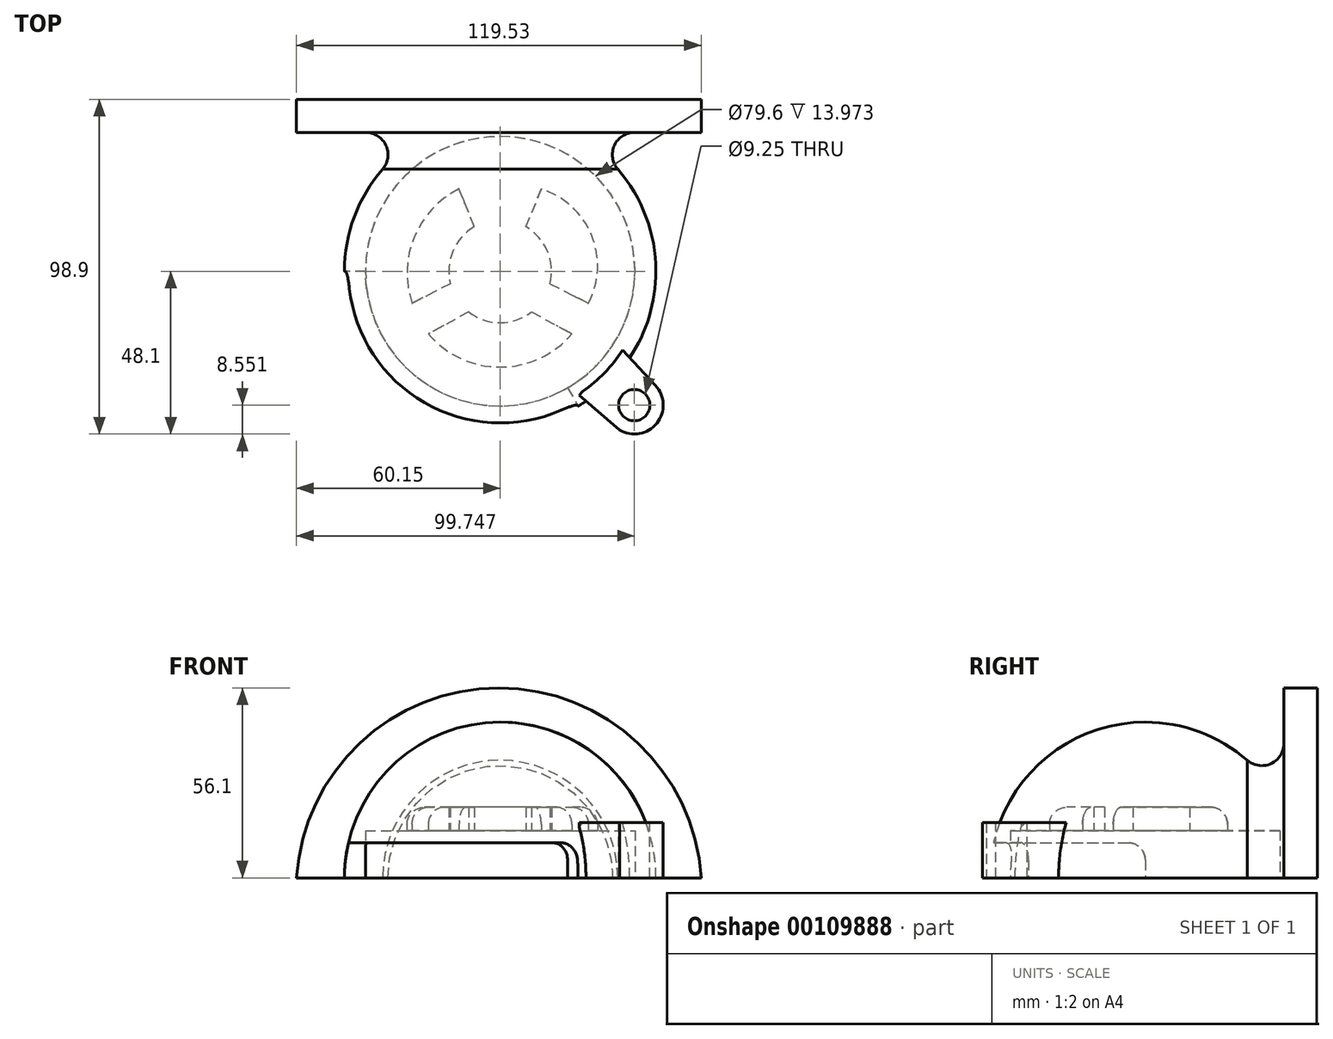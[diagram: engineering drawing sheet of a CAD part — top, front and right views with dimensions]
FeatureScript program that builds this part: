
annotation { "Feature Type Name" : "Feature", "Feature Type Description" : "" }
export const myFeature = defineFeature(function(context is Context, id is Id, definition is map)
    precondition{}
    {
        {
            var Q0;
            Q0=qCreatedBy(makeId("Front.planeOp"),FACE);
            var sketch = newSketch(context, id + "F0", { "sketchPlane" : qUnion([Q0])});
            skArc(sketch, "E0", {"start": v(46, 0) * mm, "mid": v(32.53, 32.53) * mm, "end": v(0, 46) * mm});
            skLineSegment(sketch, "E1", {"start": v(0, 41.14) * mm, "end": v(0, 46) * mm});
            skLineSegment(sketch, "E2", {"start": v(0, 70.48) * mm, "end": v(0, -35.62) * mm});
            skLineSegment(sketch, "E3", {"start": v(0, 46) * mm, "end": v(0, 0) * mm});
            skLineSegment(sketch, "E4", {"start": v(46, 0) * mm, "end": v(0, 0) * mm});
            skSolve(sketch);
        }
        {
            var Q0;
            {var subQ0=sQuery(id+"F0.wireOp",EDGE,"E0");Q0=makeQuery(id+"F0.imprint","IMPRINT",FACE,{"disambiguationData":[TD([[makeQuery(id+"F0.imprint","IMPRINT",EDGE,{"derivedFrom":subQ0}),1.0]])]});}
            var Q1;
            Q1=sQuery(id+"F0.wireOp",EDGE,"E2");
            revolve(context, id + "F1", {"entities" : qUnion([Q0]), "axis" : qUnion([Q1]), "revolveType" : RevolveType.FULL});
        }
        {
            var Q0;
            Q0=qCreatedBy(makeId("Front.planeOp"),FACE);
            var sketch = newSketch(context, id + "F2", { "sketchPlane" : qUnion([Q0])});
            skArc(sketch, "E5", {"start": v(-47.2, 10.38) * mm, "mid": v(-48.92, 3.9) * mm, "end": v(-49.05, -2.81) * mm});
            skArc(sketch, "E6", {"start": v(-36.62, 10.38) * mm, "mid": v(-39.35, 4.06) * mm, "end": v(-39.58, -2.81) * mm});
            skLineSegment(sketch, "E7", {"start": v(-36.62, 10.38) * mm, "end": v(-47.2, 10.38) * mm});
            skLineSegment(sketch, "E8", {"start": v(-39.58, -2.81) * mm, "end": v(-49.05, -2.81) * mm});
            skLineSegment(sketch, "E9", {"start": v(0, 65.03) * mm, "end": v(0, -45.95) * mm});
            skSolve(sketch);
        }
        {
            var Q0;
            Q0=makeQuery(id+"F2.imprint","IMPRINT",FACE,{"disambiguationData":[TD([[makeQuery(id+"F2.imprint","IMPRINT",EDGE,{"derivedFrom":sQuery(id+"F2.wireOp",EDGE,"E5")}),1.0]])]});
            var Q1;
            Q1=sQuery(id+"F2.wireOp",EDGE,"E9");
            revolve(context, id + "F3", {"operationType" : NewBodyOperationType.REMOVE, "entities" : qUnion([Q0]), "axis" : qUnion([Q1]), "revolveType" : RevolveType.ONE_DIRECTION, "oppositeDirection" : true, "angle" : 120 * degree});
        }
        {
            var Q0;
            Q0=makeQuery(id+"F1.opRevolve","SWEPT_FACE",FACE,{"disambiguationData":[OSD([sQuery(id+"F0.wireOp",EDGE,"E4")])]});
            var sketch = newSketch(context, id + "F4", { "sketchPlane" : qUnion([Q0])});
            skSolve(sketch);
        }
        {
            var Q0;
            {var subQ0=sQuery(id+"F0.wireOp",EDGE,"E4");Q0=makeQuery(id+"F4.imprint","IMPRINT",FACE,{"disambiguationData":[TD([[makeQuery(id+"F4.imprint","IMPRINT",EDGE,{"derivedFrom":makeQuery(id+"F1.opRevolve","SWEPT_EDGE",EDGE,{"disambiguationData":[OSD([sQuery(id+"F0.wireOp",EDGE,"E0"),subQ0])]})}),-1.0]])]});}
            var sketch = newSketch(context, id + "F5", { "sketchPlane" : qUnion([Q0])});
            skCircle(sketch, "E10", {"center": v(0, 0) * mm, "radius": 39.8 * mm});
            skSolve(sketch);
        }
        {
            var Q0;
            Q0 = qSketchRegion(id + "F5", true);
            extrude(context, id + "F6", {"entities" : qUnion([Q0]), "operationType" : NewBodyOperationType.REMOVE, "oppositeDirection" : true, "depth" : 13.97 * mm});
        }
        {
            var Q0;
            Q0=makeQuery(id+"F3.boolean.opBoolean","COPY",EDGE,{"derivedFrom":makeQuery(id+"F3.opRevolve","CAP_EDGE",EDGE,{"disambiguationData":[OSD([sQuery(id+"F2.wireOp",EDGE,"E7")])],"isStart":true})});
            var Q1;
            Q1=makeQuery(id+"F3.boolean.opBoolean","COPY",EDGE,{"derivedFrom":makeQuery(id+"F3.opRevolve","CAP_EDGE",EDGE,{"disambiguationData":[OSD([sQuery(id+"F2.wireOp",EDGE,"E7")])],"isStart":false})});
            fillet(context, id + "F7", {"entities" : qUnion([Q0, Q1]), "radius" : 5.08 * mm, "tangentPropagation" : true, "allowEdgeOverflow" : false});
        }
        {
            var Q0;
            Q0=makeQuery(id+"F6.boolean.opBoolean","COPY",FACE,{"derivedFrom":makeQuery(id+"F6.opExtrude","CAP_FACE",FACE,{"disambiguationData":[OSD([sQuery(id+"F5.wireOp",EDGE,"E10")])],"isStart":false})});
            var sketch = newSketch(context, id + "F8", { "sketchPlane" : qUnion([Q0])});
            skCircle(sketch, "E11", {"center": v(0, 0) * mm, "radius": 15.18 * mm});
            skLineSegment(sketch, "E12", {"start": v(9.26, 12.02) * mm, "end": v(21.2, 18.5) * mm});
            skLineSegment(sketch, "E13.MirrorCS", {"start": v(-9.26, 12.02) * mm, "end": v(-21.2, 18.5) * mm});
            skArc(sketch, "E14", {"start": v(21.2, 18.5) * mm, "mid": v(0, 28.3) * mm, "end": v(-21.2, 18.5) * mm});
            skLineSegment(sketch, "E15", {"start": v(14.72, 3.68) * mm, "end": v(26.03, 9.45) * mm});
            skLineSegment(sketch, "E16.MirrorCS", {"start": v(-14.72, 3.68) * mm, "end": v(-26.03, 9.45) * mm});
            skArc(sketch, "E17", {"start": v(-26.03, 9.45) * mm, "mid": v(-25.42, -10.03) * mm, "end": v(-12.15, -24.3) * mm});
            skLineSegment(sketch, "E18", {"start": v(-7.61, -13.13) * mm, "end": v(-12.15, -24.3) * mm});
            skLineSegment(sketch, "E19.MirrorCS", {"start": v(7.61, -13.13) * mm, "end": v(12.15, -24.3) * mm});
            skArc(sketch, "E20", {"start": v(12.15, -24.3) * mm, "mid": v(27, -10.68) * mm, "end": v(26.03, 9.45) * mm});
            skSolve(sketch);
        }
        {
            var Q0;
            {var subQ0=sQuery(id+"F8.wireOp",EDGE,"E12");Q0=makeQuery(id+"F8.imprint","IMPRINT",FACE,{"disambiguationData":[TD([[makeQuery(id+"F8.imprint","IMPRINT",EDGE,{"derivedFrom":subQ0}),1.0]])]});}
            var Q1;
            {var subQ0=sQuery(id+"F8.wireOp",EDGE,"E16.MirrorCS");Q1=makeQuery(id+"F8.imprint","IMPRINT",FACE,{"disambiguationData":[TD([[makeQuery(id+"F8.imprint","IMPRINT",EDGE,{"derivedFrom":subQ0}),1.0]])]});}
            var Q2;
            {var subQ0=sQuery(id+"F8.wireOp",EDGE,"E15");Q2=makeQuery(id+"F8.imprint","IMPRINT",FACE,{"disambiguationData":[TD([[makeQuery(id+"F8.imprint","IMPRINT",EDGE,{"derivedFrom":subQ0}),-1.0]])]});}
            extrude(context, id + "F9", {"entities" : qUnion([Q0, Q1, Q2]), "operationType" : NewBodyOperationType.REMOVE, "oppositeDirection" : true, "depth" : 6.89 * mm});
        }
        {
            var Q0;
            Q0=makeQuery(id+"F9.boolean.opBoolean","COPY",EDGE,{"derivedFrom":makeQuery(id+"F9.opExtrude","CAP_EDGE",EDGE,{"disambiguationData":[OSD([sQuery(id+"F8.wireOp",EDGE,"E14")])],"isStart":false})});
            var Q1;
            Q1=makeQuery(id+"F9.boolean.opBoolean","COPY",EDGE,{"derivedFrom":makeQuery(id+"F9.opExtrude","CAP_EDGE",EDGE,{"disambiguationData":[OSD([sQuery(id+"F8.wireOp",EDGE,"E20")])],"isStart":false})});
            var Q2;
            Q2=makeQuery(id+"F9.boolean.opBoolean","COPY",EDGE,{"derivedFrom":makeQuery(id+"F9.opExtrude","CAP_EDGE",EDGE,{"disambiguationData":[OSD([sQuery(id+"F8.wireOp",EDGE,"E17")])],"isStart":false})});
            fillet(context, id + "F10", {"entities" : qUnion([Q0, Q1, Q2]), "radius" : 5.08 * mm, "tangentPropagation" : true, "allowEdgeOverflow" : false});
        }
        {
            var Q0;
            Q0=qCreatedBy(makeId("Front.planeOp"),FACE);
            cPlane(context, id + "F11", {"entities" : qUnion([Q0]), "cplaneType" : CPlaneType.OFFSET, "offset" : 50.8 * mm, "oppositeDirection" : true, "width" : 152.4 * mm, "height" : 152.4 * mm});
        }
        {
            var Q0;
            Q0=qCreatedBy(id+"F11.planeOp",FACE);
            var sketch = newSketch(context, id + "F12", { "sketchPlane" : qUnion([Q0])});
            skArc(sketch, "E21", {"start": v(59.38, 0) * mm, "mid": v(-0.39, 56.1) * mm, "end": v(-60.15, 0) * mm});
            skLineSegment(sketch, "E22", {"start": v(59.38, 0) * mm, "end": v(-60.15, 0) * mm});
            skSolve(sketch);
        }
        {
            var Q0;
            Q0=makeQuery(id+"F12.imprint","IMPRINT",FACE,{"disambiguationData":[TD([[makeQuery(id+"F12.imprint","IMPRINT",EDGE,{"derivedFrom":sQuery(id+"F12.wireOp",EDGE,"E21")}),1.0]])]});
            var Q1;
            Q1=makeQuery(id+"F1.opRevolve","SWEPT_BODY",BODY,{"disambiguationData":[OSD([sQuery(id+"F0.wireOp",EDGE,"E0"),sQuery(id+"F0.wireOp",EDGE,"E3"),sQuery(id+"F0.wireOp",EDGE,"E4")])]});
            extrude(context, id + "F13", {"entities" : qUnion([Q0]), "operationType" : NewBodyOperationType.ADD, "endBoundEntityBody" : qUnion([Q1]), "depth" : 9.82 * mm});
        }
        {
            var Q0;
            Q0=makeQuery(id+"F13.boolean.opBoolean","INTERSECT",EDGE,{"derivedFrom":[makeQuery(id+"F1.opRevolve","SWEPT_FACE",FACE,{"disambiguationData":[OSD([sQuery(id+"F0.wireOp",EDGE,"E0")])]}),makeQuery(id+"F13.opExtrude","CAP_FACE",FACE,{"disambiguationData":[OSD([sQuery(id+"F12.wireOp",EDGE,"E21"),sQuery(id+"F12.wireOp",EDGE,"E22")])],"isStart":false})]});
            fillet(context, id + "F14", {"entities" : qUnion([Q0]), "radius" : 6.54 * mm, "tangentPropagation" : true, "allowEdgeOverflow" : false});
        }
        {
            var Q0;
            Q0=qCreatedBy(makeId("Top.planeOp"),FACE);
            var sketch = newSketch(context, id + "F15", { "sketchPlane" : qUnion([Q0])});
            skArc(sketch, "E23", {"start": v(32.95, -44.93) * mm, "mid": v(45.21, -46) * mm, "end": v(45.84, -33.7) * mm});
            skLineSegment(sketch, "E24", {"start": v(35.3, -46.94) * mm, "end": v(23.33, -36.69) * mm});
            skLineSegment(sketch, "E25", {"start": v(45.84, -33.7) * mm, "end": v(35.3, -22.46) * mm});
            skLineSegment(sketch, "E26", {"start": v(35.3, -22.46) * mm, "end": v(23.33, -36.69) * mm});
            skSolve(sketch);
        }
        {
            var Q0;
            {var subQ0=sQuery(id+"F15.wireOp",EDGE,"E25");Q0=makeQuery(id+"F15.imprint","IMPRINT",FACE,{"disambiguationData":[TD([[makeQuery(id+"F15.imprint","IMPRINT",EDGE,{"derivedFrom":subQ0}),1.0]])]});}
            extrude(context, id + "F16", {"entities" : qUnion([Q0]), "operationType" : NewBodyOperationType.ADD, "depth" : 16.3 * mm});
        }
        {
            var Q0;
            Q0=makeQuery(id+"F16.opExtrude","CAP_FACE",FACE,{"disambiguationData":[OSD([sQuery(id+"F15.wireOp",EDGE,"E23"),sQuery(id+"F15.wireOp",EDGE,"E24"),sQuery(id+"F15.wireOp",EDGE,"E25"),sQuery(id+"F15.wireOp",EDGE,"E26")])],"isStart":false});
            var sketch = newSketch(context, id + "F17", { "sketchPlane" : qUnion([Q0])});
            skCircle(sketch, "E27", {"center": v(39.6, -39.55) * mm, "radius": 4.62 * mm});
            skSolve(sketch);
        }
        {
            var Q0;
            Q0=makeQuery(id+"F17.imprint","IMPRINT",FACE,{"disambiguationData":[TD([[makeQuery(id+"F17.imprint","IMPRINT",EDGE,{"derivedFrom":sQuery(id+"F17.wireOp",EDGE,"E27")}),1.0]])]});
            extrude(context, id + "F18", {"entities" : qUnion([Q0]), "operationType" : NewBodyOperationType.REMOVE, "oppositeDirection" : true, "depth" : 25.4 * mm});
        }
    });
